# Revit family: BROWNLEE - 5165 - FLOW SQUARE -13
name_source: partatom
category: Lighting Fixtures
revit_build: Autodesk Revit 2017 (Build: 20160225_1515(x64)
units: mm (PartAtom-declared; Revit-internal decimal feet)

## family parameters
Cut with Voids When Loaded = No
Host = Face
Light Source = Yes
Part Type = Normal
Room Calculation Point = No
Round Connector Dimension = Use Diameter
Shared = No

## types (2) — shared parameters
Color Filter = 16777215
Default Elevation = 4' - 0"
Description = Contemporary ultra slim square light bar, Dimmable
Dimming Lamp Color Temperature Shift = <None>
Emit from Line Length = 2' - 0"
Lens = BROWLEE LIGHTING - ACRYLIC LENS
Manufacturer = Brownlee Lighting
Metal Finish = BROWNLEE LIGHTING - FINISH - BRUSHED NICKEL
Tilt Angle = 0.00°
URL = www.brownlee.com

## per-type parameters (varying)
| type | Model | Photometric Web File |
| 5165-13-H08-35K | 5165-13-BN-H08-35K | 5165-13-H08-35K.IES |
| 5165-13-H10-35K | 5165-13-BN-H10-35K | 5165-13-H10-35K.ies |

## geometry (parser evidence)
native form markers: Sweep x3
no freeform markers — native parametric forms only
